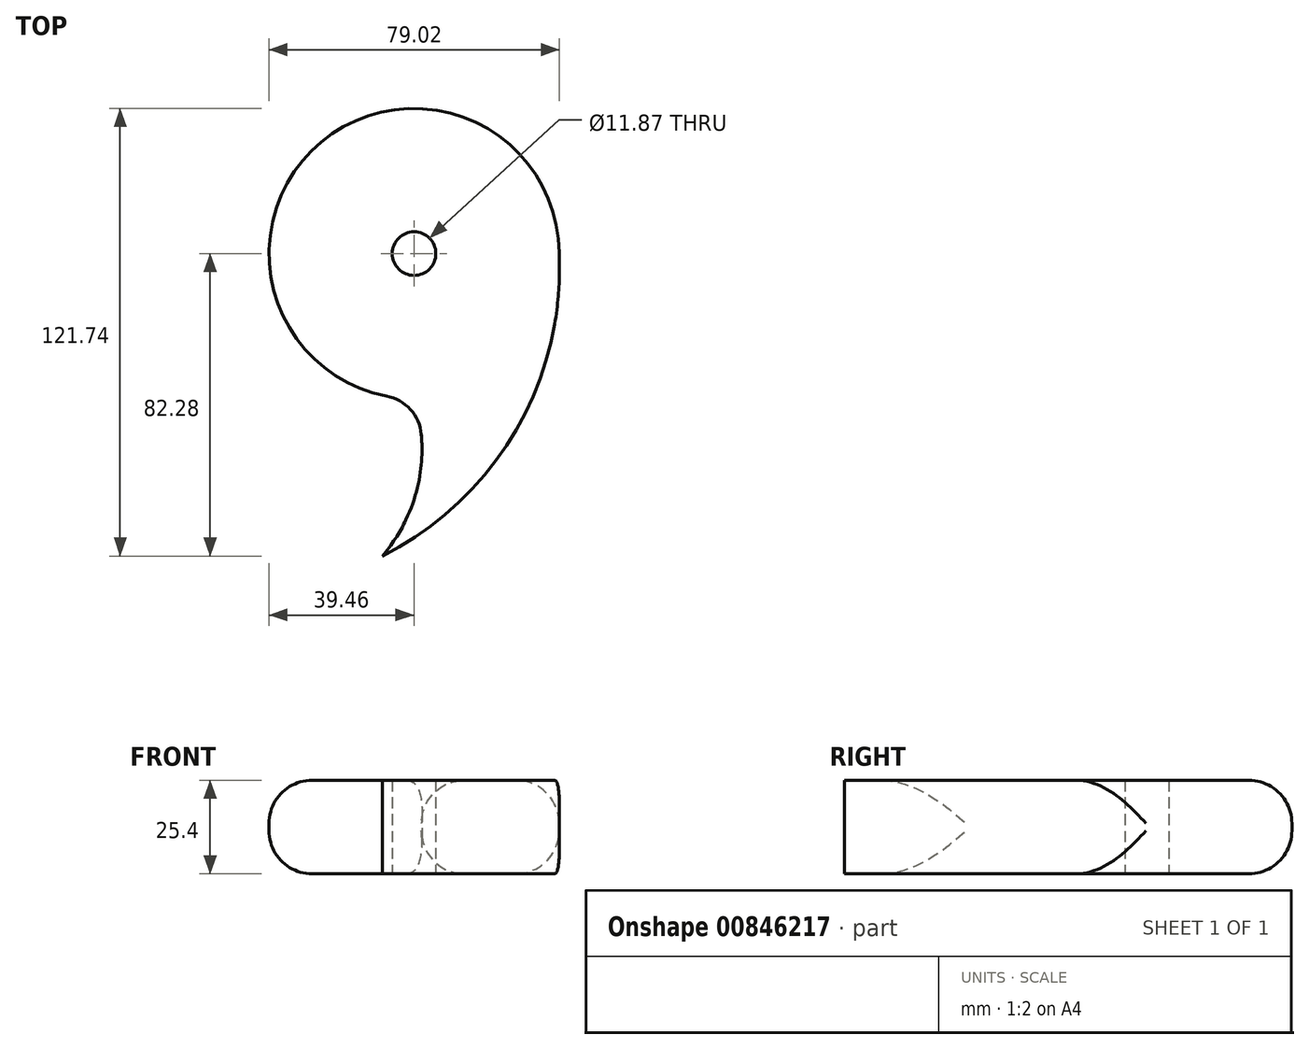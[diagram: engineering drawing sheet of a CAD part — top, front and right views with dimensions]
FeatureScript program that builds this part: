
annotation { "Feature Type Name" : "Feature", "Feature Type Description" : "" }
export const myFeature = defineFeature(function(context is Context, id is Id, definition is map)
    precondition{}
    {
        {
            var Q0;
            Q0=qCreatedBy(makeId("Top.planeOp"),FACE);
            var sketch = newSketch(context, id + "F0", { "sketchPlane" : qUnion([Q0])});
            skArc(sketch, "E0", {"start": v(39.46, 0) * mm, "mid": v(-27.9, 27.9) * mm, "end": v(0, -39.46) * mm});
            skPoint(sketch, "E1.orphan", {"position": v(0, -74.06) * mm});
            skArc(sketch, "E2", {"start": v(-10.37, -84.19) * mm, "mid": v(1, -63.26) * mm, "end": v(0, -39.46) * mm});
            skArc(sketch, "E3", {"start": v(-8.63, -82.28) * mm, "mid": v(27.61, -48.27) * mm, "end": v(39.46, 0) * mm});
            skSolve(sketch);
        }
        {
            var Q0;
            Q0=qSketchRegion(id+"F0",true);
            extrude(context, id + "F1", {"entities" : qUnion([Q0]), "depth" : 25.4 * mm, "offsetDistance" : 25.4 * mm});
        }
        {
            var Q0;
            Q0=qCreatedBy(makeId("Top.planeOp"),FACE);
            var sketch = newSketch(context, id + "F2", { "sketchPlane" : qUnion([Q0])});
            skCircle(sketch, "E4", {"center": v(0, 0) * mm, "radius": 5.93 * mm});
            skSolve(sketch);
        }
        {
            var Q0;
            Q0=qSketchRegion(id+"F2",true);
            extrude(context, id + "F3", {"entities" : qUnion([Q0]), "operationType" : NewBodyOperationType.REMOVE, "depth" : 25.4 * mm, "offsetDistance" : 25.4 * mm});
        }
        {
            var Q0;
            Q0=makeQuery(id+"F1.opExtrude","SWEPT_FACE",FACE,{"disambiguationData":[OSD([sQuery(id+"F0.wireOp",EDGE,"E0")])]});
            fillet(context, id + "F4", {"entities" : qUnion([Q0]), "radius" : 11.7 * mm, "tangentPropagation" : true, "allowEdgeOverflow" : false});
        }
    });
